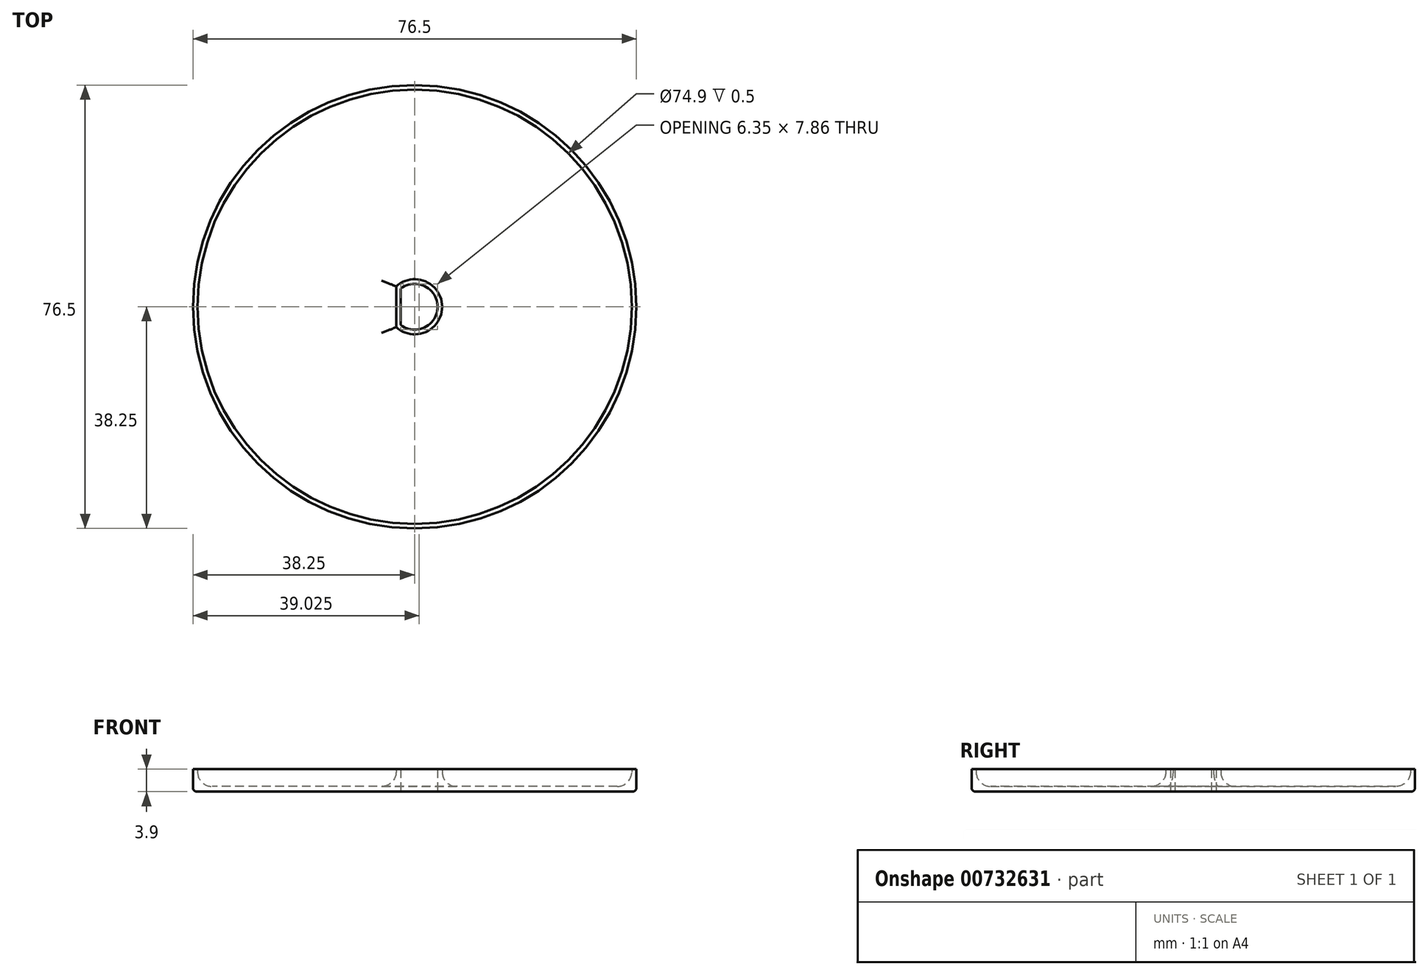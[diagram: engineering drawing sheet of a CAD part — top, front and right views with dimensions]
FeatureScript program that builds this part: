
annotation { "Feature Type Name" : "Feature", "Feature Type Description" : "" }
export const myFeature = defineFeature(function(context is Context, id is Id, definition is map)
    precondition{}
    {
        {
            var Q0;
            Q0=qCreatedBy(makeId("Top.planeOp"),FACE);
            var sketch = newSketch(context, id + "F0", { "sketchPlane" : qUnion([Q0])});
            skCircle(sketch, "E0", {"center": v(0, 0) * mm, "radius": 38.25 * mm});
            skCircle(sketch, "E1", {"center": v(0, 0) * mm, "radius": 3.95 * mm});
            skLineSegment(sketch, "E2", {"start": v(-2.4, 3.14) * mm, "end": v(-2.4, -3.14) * mm});
            skLineSegment(sketch, "E3", {"start": v(2.4, 3.14) * mm, "end": v(2.4, -3.14) * mm});
            skSolve(sketch);
        }
        {
            var Q0;
            Q0=makeQuery(id+"F0.imprint","IMPRINT",FACE,{"disambiguationData":[TD([[makeQuery(id+"F0.imprint","IMPRINT",EDGE,{"derivedFrom":sQuery(id+"F0.wireOp",EDGE,"E0")}),1.0]])]});
            var Q1;
            {var subQ0=sQuery(id+"F0.wireOp",EDGE,"E2");Q1=makeQuery(id+"F0.imprint","IMPRINT",FACE,{"disambiguationData":[TD([[makeQuery(id+"F0.imprint","IMPRINT",EDGE,{"derivedFrom":subQ0}),-1.0]])]});}
            extrude(context, id + "F1", {"entities" : qUnion([Q0, Q1]), "depth" : 0.9 * mm, "offsetDistance" : 25 * mm});
        }
        {
            var Q0;
            Q0=makeQuery(id+"F1.opExtrude","CAP_FACE",FACE,{"disambiguationData":[OSD([sQuery(id+"F0.wireOp",EDGE,"E0"),sQuery(id+"F0.wireOp",EDGE,"E1"),sQuery(id+"F0.wireOp",EDGE,"E2")])],"isStart":false});
            var sketch = newSketch(context, id + "F2", { "sketchPlane" : qUnion([Q0])});
            skArc(sketch, "E4.0", {"start": v(-3.2, -3.51) * mm, "mid": v(4.75, 0) * mm, "end": v(-3.2, 3.51) * mm});
            skLineSegment(sketch, "E4.1", {"start": v(-3.2, 3.51) * mm, "end": v(-3.2, -3.51) * mm});
            skCircle(sketch, "E5.0", {"center": v(0, 0) * mm, "radius": 37.45 * mm});
            skSolve(sketch);
        }
        {
            var Q0;
            Q0=makeQuery(id+"F2.imprint","IMPRINT",FACE,{"disambiguationData":[TD([[makeQuery(id+"F2.imprint","IMPRINT",EDGE,{"derivedFrom":sQuery(id+"F2.wireOp",EDGE,"E4.0")}),1.0]])]});
            var Q1;
            Q1=makeQuery(id+"F2.imprint","IMPRINT",FACE,{"disambiguationData":[TD([[makeQuery(id+"F2.imprint","IMPRINT",EDGE,{"derivedFrom":sQuery(id+"F2.wireOp",EDGE,"E5.0")}),-1.0]])]});
            extrude(context, id + "F3", {"entities" : qUnion([Q0, Q1]), "operationType" : NewBodyOperationType.ADD, "depth" : 3 * mm, "offsetDistance" : 25 * mm});
        }
        {
            var Q0;
            Q0=makeQuery(id+"F1.opExtrude","CAP_FACE",FACE,{"disambiguationData":[OSD([sQuery(id+"F0.wireOp",EDGE,"E0"),sQuery(id+"F0.wireOp",EDGE,"E1"),sQuery(id+"F0.wireOp",EDGE,"E2")])],"isStart":false});
            fillet(context, id + "F4", {"entities" : qUnion([Q0]), "radius" : 2.5 * mm, "tangentPropagation" : true, "allowEdgeOverflow" : false});
        }
        {
            var Q0;
            Q0=makeQuery(id+"F1.opExtrude","CAP_EDGE",EDGE,{"disambiguationData":[OSD([sQuery(id+"F0.wireOp",EDGE,"E0")])],"isStart":true});
            fillet(context, id + "F5", {"entities" : qUnion([Q0]), "radius" : 0.7 * mm, "tangentPropagation" : true, "allowEdgeOverflow" : false});
        }
    });
